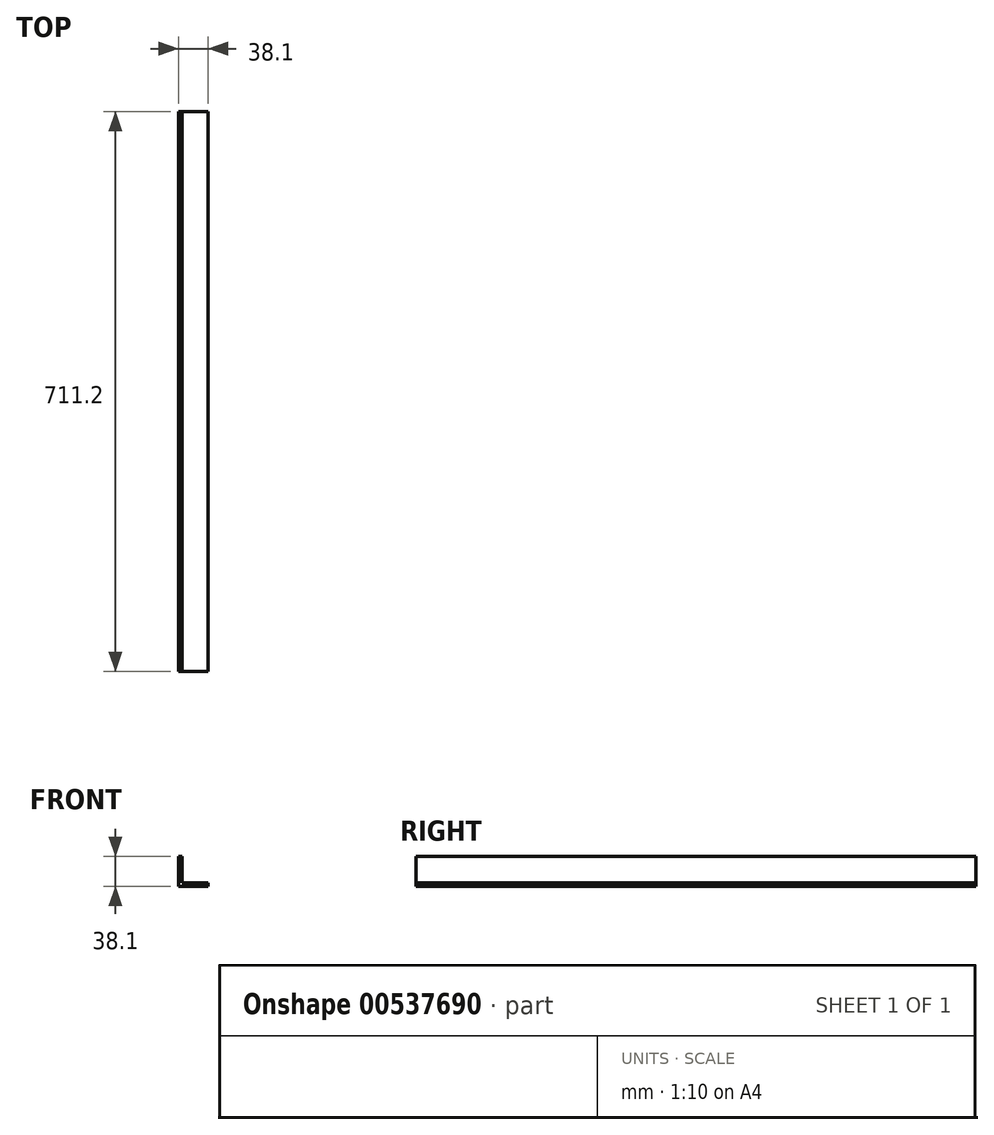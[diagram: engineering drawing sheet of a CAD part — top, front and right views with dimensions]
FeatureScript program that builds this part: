
annotation { "Feature Type Name" : "Feature", "Feature Type Description" : "" }
export const myFeature = defineFeature(function(context is Context, id is Id, definition is map)
    precondition{}
    {
        {
            var Q0;
            Q0=qCreatedBy(makeId("Front.planeOp"),FACE);
            var sketch = newSketch(context, id + "F0", { "sketchPlane" : qUnion([Q0])});
            skLineSegment(sketch, "E0", {"start": v(0, 0) * mm, "end": v(0, 38.1) * mm});
            skLineSegment(sketch, "E1", {"start": v(0, 38.1) * mm, "end": v(4.76, 38.1) * mm});
            skLineSegment(sketch, "E2", {"start": v(4.76, 38.1) * mm, "end": v(4.76, 4.76) * mm});
            skLineSegment(sketch, "E3", {"start": v(4.76, 4.76) * mm, "end": v(38.1, 4.76) * mm});
            skLineSegment(sketch, "E4", {"start": v(38.1, 4.76) * mm, "end": v(38.1, 0) * mm});
            skLineSegment(sketch, "E5", {"start": v(38.1, 0) * mm, "end": v(0, 0) * mm});
            skSolve(sketch);
        }
        {
            var Q0;
            Q0 = qSketchRegion(id + "F0", true);
            extrude(context, id + "F1", {"entities" : qUnion([Q0]), "oppositeDirection" : true, "depth" : 711.2 * mm, "offsetDistance" : 25.4 * mm});
        }
    });
